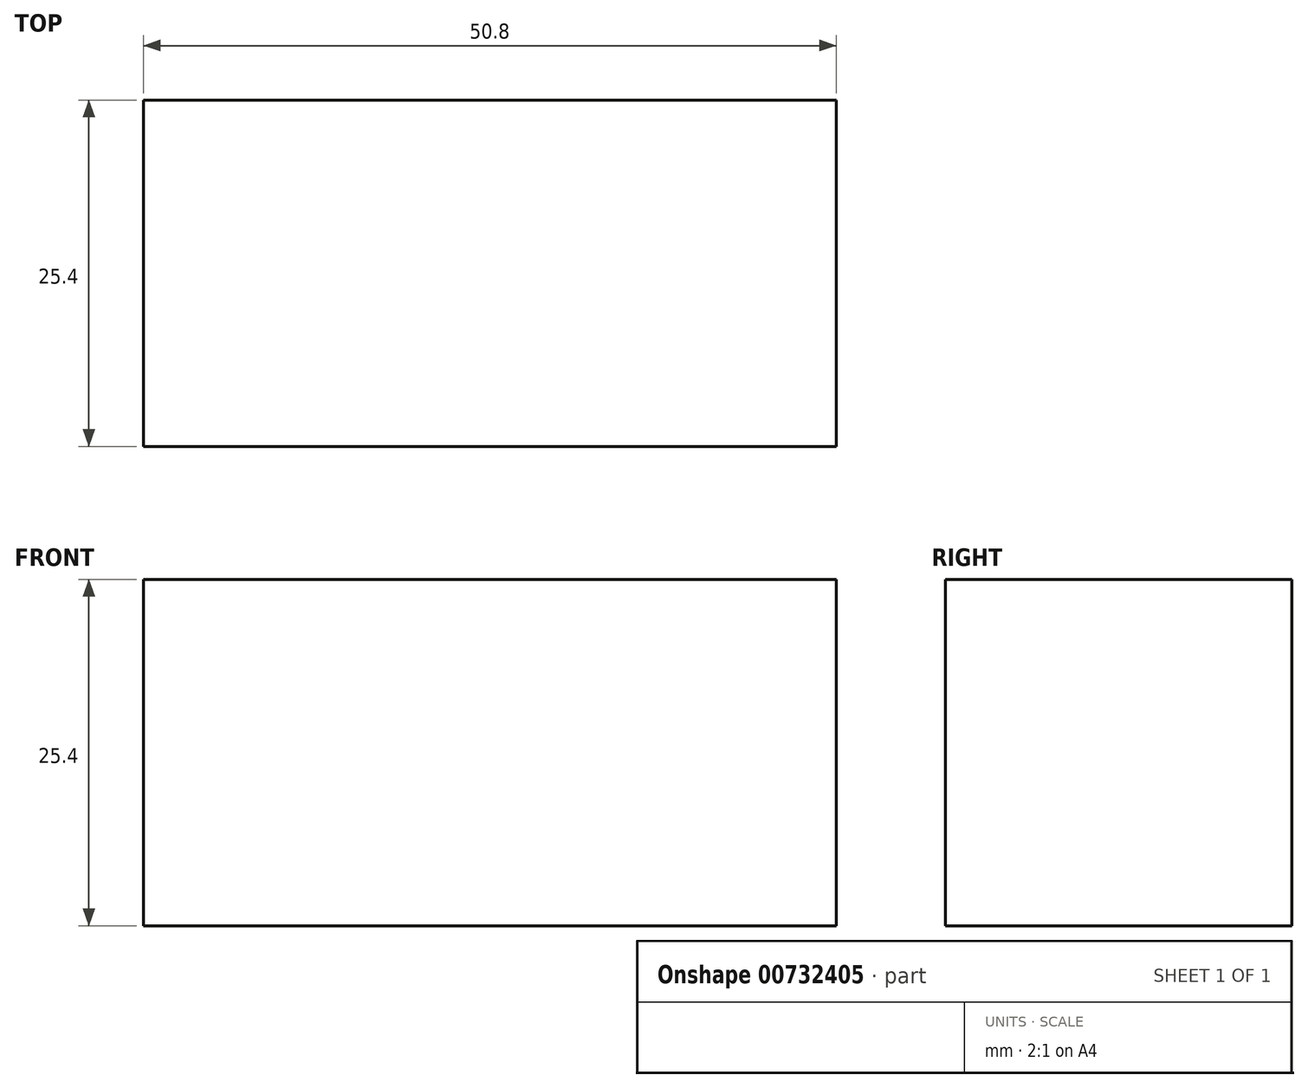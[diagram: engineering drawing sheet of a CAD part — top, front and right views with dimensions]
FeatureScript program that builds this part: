
annotation { "Feature Type Name" : "Feature", "Feature Type Description" : "" }
export const myFeature = defineFeature(function(context is Context, id is Id, definition is map)
    precondition{}
    {
        {
            var Q0;
            Q0=qCreatedBy(makeId("Top.planeOp"),FACE);
            var sketch = newSketch(context, id + "F0", { "sketchPlane" : qUnion([Q0])});
            skLineSegment(sketch, "E0.bottom", {"start": v(0, 0) * mm, "end": v(50.8, 0) * mm});
            skLineSegment(sketch, "E0.top", {"start": v(0, 25.4) * mm, "end": v(50.8, 25.4) * mm});
            skLineSegment(sketch, "E0.left", {"start": v(0, 0) * mm, "end": v(0, 25.4) * mm});
            skLineSegment(sketch, "E0.right", {"start": v(50.8, 0) * mm, "end": v(50.8, 25.4) * mm});
            skSolve(sketch);
        }
        {
            var Q0;
            Q0=makeQuery(id+"F0.imprint","IMPRINT",FACE,{"disambiguationData":[TD([[makeQuery(id+"F0.imprint","IMPRINT",EDGE,{"derivedFrom":sQuery(id+"F0.wireOp",EDGE,"E0.bottom")}),1.0]])]});
            extrude(context, id + "F1", {"entities" : qUnion([Q0]), "depth" : 25.4 * mm, "offsetDistance" : 25.4 * mm});
        }
    });
